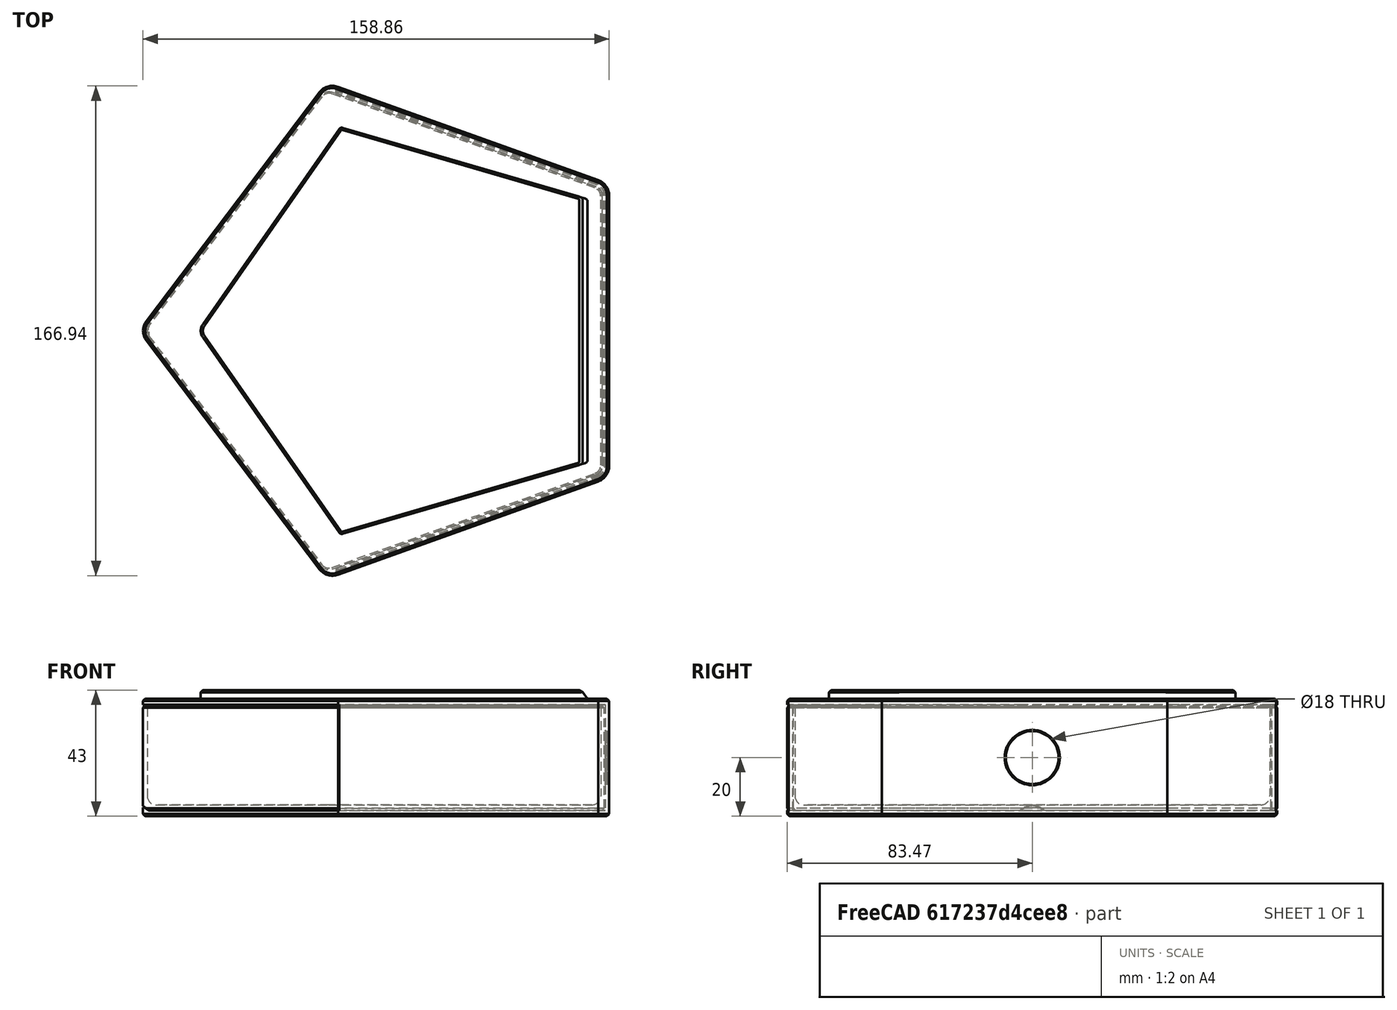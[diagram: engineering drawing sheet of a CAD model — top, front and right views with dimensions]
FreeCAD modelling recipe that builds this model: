
FCSTD DOCUMENT  (FreeCAD 1.0R39109 (Git))
Label: storage box
License: All rights reserved
objects: Sketcher::SketchObject×11, PartDesign::Pocket×6, PartDesign::Chamfer×6, PartDesign::Pad×5, PartDesign::SubShapeBinder×3, PartDesign::Fillet×2, PartDesign::Body×2, Mesh::Feature×1, Part::Feature×1, App::VarSet×1
note: 85 computed .brp shape members not serialized (recipe doc carries the construction recipe); baked Part::Feature solids carry a one-line shape summary decoded from their .brp

FEATURE [Mesh::Feature] stand
FEATURE [Part::Feature] stand001
  shape: bbox 160.2 x 168.2 x 43.41 mm, 6068 faces, 0 solids (baked)
FEATURE [Sketcher::SketchObject] Sketch  label="stand_footprint"
  ArcFitTolerance = 1e-06
  ExternalGeometry = -> [stand001]
  FullyConstrained = true
  MakeInternals = false
  sketch-geometry (17):
    g0: Circle [constr] CenterX=106.078 CenterY=95.15 CenterZ=0 NormalX=0 NormalY=0 NormalZ=1 AngleXU=0 Radius=73.5295
    g1: LineSegment StartX=82.4481 StartY=164.779 StartZ=0 EndX=35.3147 EndY=97.3554 EndZ=0
    g2: LineSegment StartX=35.3147 StartY=92.9447 StartZ=0 EndX=82.4481 EndY=25.521 EndZ=0
    g3: LineSegment StartX=82.4481 StartY=25.521 StartZ=0 EndX=166.952 EndY=50.1585 EndZ=0
    g4: LineSegment StartX=166.952 StartY=50.1585 StartZ=0 EndX=166.952 EndY=140.142 EndZ=0
    g5: LineSegment StartX=166.952 StartY=140.142 StartZ=0 EndX=82.4481 EndY=164.779 EndZ=0
    g6: ArcOfCircle CenterX=38.8397 CenterY=95.15 CenterZ=0 NormalX=0 NormalY=0 NormalZ=1 AngleXU=0 Radius=4.15798 StartAngle=2.58254 EndAngle=3.70065
    g7: LineSegment StartX=81.6615 StartY=178.264 StartZ=0 EndX=170.408 EndY=146.468 EndZ=0
    g8: LineSegment StartX=174.094 StartY=141.161 StartZ=0 EndX=174.094 EndY=49.139 EndZ=0
    g9: LineSegment StartX=170.408 StartY=43.8321 StartZ=0 EndX=81.6615 EndY=12.0355 EndZ=0
    g10: LineSegment StartX=75.409 StartY=13.8037 StartZ=0 EndX=16.3247 EndY=91.9295 EndZ=0
    g11: LineSegment StartX=16.3247 StartY=98.3706 StartZ=0 EndX=75.409 EndY=176.496 EndZ=0
    g12: ArcOfCircle CenterX=20.5106 CenterY=95.15 CenterZ=0 NormalX=0 NormalY=0 NormalZ=1 AngleXU=0 Radius=5.28138 StartAngle=2.4858 EndAngle=3.79739
    g13: ArcOfCircle CenterX=79.7221 CenterY=173.184 CenterZ=0 NormalX=0 NormalY=0 NormalZ=1 AngleXU=0 Radius=5.43855 StartAngle=1.20616 EndAngle=2.48661
    g14: ArcOfCircle CenterX=168.527 CenterY=141.227 CenterZ=0 NormalX=0 NormalY=0 NormalZ=1 AngleXU=0 Radius=5.56815 StartAngle=6.27131 EndAngle=7.50937
    g15: ArcOfCircle CenterX=168.451 CenterY=49.1255 CenterZ=0 NormalX=0 NormalY=0 NormalZ=1 AngleXU=0 Radius=5.64348 StartAngle=5.06648 EndAngle=6.28558
    g16: ArcOfCircle CenterX=79.7195 CenterY=17.1072 CenterZ=0 NormalX=0 NormalY=0 NormalZ=1 AngleXU=0 Radius=5.43077 StartAngle=3.7955 EndAngle=5.07809
  constraints (41):
    c: PointOnObject(g-7,g0)
    c: Coincident(g1,g-5)
    c: Coincident(g2,g-7)
    c: Coincident(g3,g2)
    c: Coincident(g3,g-7)
    c: Coincident(g4,g3)
    c: Coincident(g4,g-5)
    c: Coincident(g5,g4)
    c: Coincident(g5,g1)
    c: Coincident(g2,g-6)
    c: Coincident(g1,g-8)
    c: Coincident(g6,g1)
    c: Coincident(g6,g2)
    c: PointOnObject(g-9,g6)
    c: Coincident(g7,g-16)
    c: Coincident(g7,g-17)
    c: Coincident(g8,g-18)
    c: Coincident(g8,g-19)
    c: Coincident(g9,g-10)
    c: Coincident(g9,g-11)
    c: Coincident(g10,g-12)
    c: Coincident(g10,g-13)
    c: Tangent(g10,g0)
    c: Coincident(g11,g-14)
    c: Coincident(g11,g-15)
    c: Tangent(g11,g0)
    c: Coincident(g12,g10)
    c: Coincident(g12,g11)
    c: PointOnObject(g-24,g12)
    c: Coincident(g13,g11)
    c: Coincident(g13,g7)
    c: PointOnObject(g-20,g13)
    c: Coincident(g14,g7)
    c: Coincident(g14,g8)
    c: PointOnObject(g-21,g14)
    c: Coincident(g15,g9)
    c: Coincident(g15,g8)
    c: PointOnObject(g-22,g15)
    c: Coincident(g16,g10)
    c: Coincident(g16,g9)
    c: PointOnObject(g-23,g16)
FEATURE [Sketcher::SketchObject] Sketch001
  ArcFitTolerance = 1e-06
  AttachmentSupport = -> [XY_Plane]
  ExternalGeometry = -> [stand001]
  FullyConstrained = true
  MakeInternals = false
  MapMode = 5
  sketch-geometry (11):
    g0: Circle [constr] CenterX=106.078 CenterY=95.15 CenterZ=0 NormalX=0 NormalY=0 NormalZ=1 AngleXU=0 Radius=73.5295
    g1: LineSegment StartX=81.6615 StartY=178.264 StartZ=0 EndX=170.408 EndY=146.468 EndZ=0
    g2: LineSegment StartX=174.094 StartY=141.161 StartZ=0 EndX=174.094 EndY=49.139 EndZ=0
    g3: LineSegment StartX=170.408 StartY=43.8321 StartZ=0 EndX=81.6615 EndY=12.0355 EndZ=0
    g4: LineSegment StartX=75.409 StartY=13.8037 StartZ=0 EndX=16.3247 EndY=91.9295 EndZ=0
    g5: LineSegment StartX=16.3247 StartY=98.3706 StartZ=0 EndX=75.409 EndY=176.496 EndZ=0
    g6: ArcOfCircle CenterX=20.5106 CenterY=95.15 CenterZ=0 NormalX=0 NormalY=0 NormalZ=1 AngleXU=0 Radius=5.28138 StartAngle=2.4858 EndAngle=3.79739
    g7: ArcOfCircle CenterX=79.7221 CenterY=173.184 CenterZ=0 NormalX=0 NormalY=0 NormalZ=1 AngleXU=0 Radius=5.43855 StartAngle=1.20616 EndAngle=2.48661
    g8: ArcOfCircle CenterX=168.527 CenterY=141.227 CenterZ=0 NormalX=0 NormalY=0 NormalZ=1 AngleXU=0 Radius=5.56815 StartAngle=6.27131 EndAngle=7.50937
    g9: ArcOfCircle CenterX=168.451 CenterY=49.1255 CenterZ=0 NormalX=0 NormalY=0 NormalZ=1 AngleXU=0 Radius=5.64348 StartAngle=5.06648 EndAngle=6.28558
    g10: ArcOfCircle CenterX=79.7195 CenterY=17.1072 CenterZ=0 NormalX=0 NormalY=0 NormalZ=1 AngleXU=0 Radius=5.43077 StartAngle=3.7955 EndAngle=5.07809
  constraints (28):
    c: PointOnObject(g-7,g0)
    c: Coincident(g1,g-16)
    c: Coincident(g1,g-17)
    c: Coincident(g2,g-18)
    c: Coincident(g2,g-19)
    c: Coincident(g3,g-10)
    c: Coincident(g3,g-11)
    c: Coincident(g4,g-12)
    c: Coincident(g4,g-13)
    c: Tangent(g4,g0)
    c: Coincident(g5,g-14)
    c: Coincident(g5,g-15)
    c: Tangent(g5,g0)
    c: Coincident(g6,g4)
    c: Coincident(g6,g5)
    c: PointOnObject(g-24,g6)
    c: Coincident(g7,g5)
    c: Coincident(g7,g1)
    c: PointOnObject(g-20,g7)
    c: Coincident(g8,g1)
    c: Coincident(g8,g2)
    c: PointOnObject(g-21,g8)
    c: Coincident(g9,g3)
    c: Coincident(g9,g2)
    c: PointOnObject(g-22,g9)
    c: Coincident(g10,g4)
    c: Coincident(g10,g3)
    c: PointOnObject(g-23,g10)
FEATURE [App::VarSet] VarSet001  label="dim"
  Height = 40
  back_hole = 18
  lip_height = 3
  wall = 1.3
FEATURE [PartDesign::Pad] Pad
  Direction = (0,0,1)
  Length = 40
  Length2 = 10
  Profile = -> Sketch001
  ReferenceAxis = -> Sketch001 [N_Axis]
  Refine = true
  Reversed = true
  Suppressed = false
  Type = 0
  expr: Length = VarSet001.Height
FEATURE [Sketcher::SketchObject] Sketch002
  ArcFitTolerance = 1e-06
  AttachmentSupport = -> [XY_Plane]
  ExternalGeometry = -> [stand001]
  FullyConstrained = true
  MakeInternals = false
  MapMode = 5
  sketch-geometry (20):
    g0: LineSegment [constr] StartX=82.4481 StartY=164.779 StartZ=0 EndX=35.3147 EndY=97.3554 EndZ=0
    g1: LineSegment [constr] StartX=35.3147 StartY=92.9447 StartZ=0 EndX=82.4481 EndY=25.521 EndZ=0
    g2: LineSegment [constr] StartX=82.4481 StartY=25.521 StartZ=0 EndX=166.952 EndY=50.1585 EndZ=0
    g3: LineSegment [constr] StartX=166.952 StartY=50.1585 StartZ=0 EndX=166.952 EndY=140.142 EndZ=0
    g4: ArcOfCircle [constr] CenterX=38.8397 CenterY=95.15 CenterZ=0 NormalX=0 NormalY=0 NormalZ=1 AngleXU=0 Radius=4.15798 StartAngle=2.58254 EndAngle=3.70065
    g5: LineSegment [constr] StartX=82.4481 StartY=164.779 StartZ=0 EndX=166.952 EndY=140.142 EndZ=0
    g6: LineSegment StartX=82.5298 StartY=164.547 StartZ=0 EndX=166.752 EndY=139.991 EndZ=0
    g7: LineSegment StartX=166.752 StartY=50.3085 StartZ=0 EndX=166.752 EndY=139.991 EndZ=0
    g8: LineSegment StartX=82.5298 StartY=25.7532 StartZ=0 EndX=166.752 EndY=50.3085 EndZ=0
    g9: LineSegment StartX=35.6002 StartY=92.8854 StartZ=0 EndX=82.5298 EndY=25.7532 EndZ=0
    g10: ArcOfCircle CenterX=38.8397 CenterY=95.15 CenterZ=0 NormalX=0 NormalY=0 NormalZ=1 AngleXU=0 Radius=3.95256 StartAngle=2.5315 EndAngle=3.75169
    g11: LineSegment StartX=82.5298 StartY=164.547 StartZ=0 EndX=35.6002 EndY=97.4146 EndZ=0
    g12: LineSegment [constr] StartX=166.752 StartY=139.991 StartZ=0 EndX=166.952 EndY=139.991 EndZ=0
    g13: LineSegment [constr] StartX=166.752 StartY=139.991 StartZ=0 EndX=166.808 EndY=140.183 EndZ=0
    g14: LineSegment [constr] StartX=82.5298 StartY=164.547 StartZ=0 EndX=82.5858 EndY=164.739 EndZ=0
    g15: LineSegment [constr] StartX=82.5298 StartY=164.547 StartZ=0 EndX=82.3659 EndY=164.661 EndZ=0
    g16: LineSegment [constr] StartX=166.752 StartY=50.3085 StartZ=0 EndX=166.952 EndY=50.3085 EndZ=0
    g17: LineSegment [constr] StartX=166.752 StartY=50.3085 StartZ=0 EndX=166.808 EndY=50.1165 EndZ=0
    g18: LineSegment [constr] StartX=82.5298 StartY=25.7532 StartZ=0 EndX=82.5858 EndY=25.5612 EndZ=0
    g19: LineSegment [constr] StartX=82.5298 StartY=25.7532 StartZ=0 EndX=82.3659 EndY=25.6386 EndZ=0
  constraints (53):
    c: Coincident(g1,g-6)
    c: Coincident(g2,g1)
    c: Coincident(g3,g-4)
    c: Coincident(g1,g-5)
    c: Coincident(g0,g-7)
    c: Coincident(g4,g0)
    c: Coincident(g4,g1)
    c: PointOnObject(g-8,g4)
    c: Coincident(g5,g0)
    c: Coincident(g5,g3)
    c: Coincident(g0,g-7)
    c: Coincident(g6,g7)
    c: Coincident(g6,g11)
    c: Coincident(g7,g8)
    c: Coincident(g8,g9)
    c: Coincident(g12,g6)
    c: PointOnObject(g12,g3)
    c: Perpendicular(g3,g12)
    c: Distance(g12,g12) = 0.2
    c: Coincident(g13,g6)
    c: PointOnObject(g13,g5)
    c: Perpendicular(g5,g13)
    c: Equal(g13,g12)
    c: Parallel(g6,g5)
    c: Parallel(g11,g0)
    c: Coincident(g14,g6)
    c: PointOnObject(g14,g5)
    c: Coincident(g15,g6)
    c: PointOnObject(g15,g0)
    c: Perpendicular(g15,g0)
    c: Perpendicular(g5,g14)
    c: Equal(g14,g15)
    c: Parallel(g3,g7)
    c: Coincident(g16,g7)
    c: PointOnObject(g16,g3)
    c: Horizontal(g16)
    c: Coincident(g17,g7)
    c: PointOnObject(g17,g2)
    c: Perpendicular(g2,g17)
    c: Equal(g17,g16)
    c: Parallel(g8,g2)
    c: Parallel(g9,g1)
    c: Coincident(g2,g3)
    c: Coincident(g2,g-6)
    c: Coincident(g18,g8)
    c: PointOnObject(g18,g2)
    c: Coincident(g19,g8)
    c: PointOnObject(g19,g1)
    c: Perpendicular(g19,g1)
    c: Perpendicular(g2,g18)
    c: Coincident(g4,g10)
    c: Tangent(g9,g10) = -1.5708
    c: Tangent(g10,g11) = -1.5708
FEATURE [PartDesign::Pad] Pad001
  BaseFeature = -> Pad
  Direction = (0,0,1)
  Length = 3
  Length2 = 10
  Profile = -> Sketch002
  ReferenceAxis = -> Sketch002 [N_Axis]
  Refine = true
  Suppressed = false
  Type = 0
  expr: Length = VarSet001.lip_height
FEATURE [Sketcher::SketchObject] Sketch003
  ArcFitTolerance = 1e-06
  AttachmentOffset = pos=(0,0,-2) rot=(0,0,1;0rad)
  FullyConstrained = true
  MakeInternals = false
  MapMode = 5
  Placement = pos=(0,0,-38) rot=(1,0,0;3.14159rad)
  expr: Constraints[27] = VarSet001.wall
  sketch-geometry (14):
    g0: LineSegment StartX=81.6615 StartY=-3.49618 StartZ=0 EndX=81.6615 EndY=-13.4962 EndZ=0
    g1: LineSegment StartX=81.6615 StartY=-13.4962 StartZ=0 EndX=169.891 EndY=-45.1074 EndZ=0
    g2: LineSegment StartX=172.719 StartY=-49.122 StartZ=0 EndX=172.795 EndY=-141.224 EndZ=0
    g3: LineSegment StartX=169.966 StartY=-145.245 StartZ=0 EndX=81.6615 EndY=-176.884 EndZ=0
    g4: LineSegment StartX=81.6615 StartY=-176.884 StartZ=0 EndX=81.6615 EndY=-186.884 EndZ=0
    g5: LineSegment StartX=81.6615 StartY=-186.884 StartZ=0 EndX=0 EndY=-186.884 EndZ=0
    g6: LineSegment StartX=0 StartY=-186.884 StartZ=0 EndX=0 EndY=-3.49618 EndZ=0
    g7: LineSegment StartX=0 StartY=-3.49618 StartZ=0 EndX=81.6615 EndY=-3.49618 EndZ=0
    g8: ArcOfCircle CenterX=168.527 CenterY=-141.227 CenterZ=0 NormalX=0 NormalY=0 NormalZ=1 AngleXU=0 Radius=4.26815 StartAngle=5.05643 EndAngle=6.28401
    g9: GeomPoint [constr] X=172.797 Y=-144.231 Z=0
    g10: ArcOfCircle CenterX=168.451 CenterY=-49.1255 CenterZ=0 NormalX=0 NormalY=0 NormalZ=1 AngleXU=0 Radius=4.26815 StartAngle=0.000821981 EndAngle=1.22676
    g11: GeomPoint [constr] X=172.717 Y=-46.12 Z=0
    g12: LineSegment [constr] StartX=81.6615 StartY=-176.884 StartZ=0 EndX=81.6615 EndY=-178.264 EndZ=0
    g13: LineSegment [constr] StartX=81.6615 StartY=-176.884 StartZ=0 EndX=82.1 EndY=-178.107 EndZ=0
  constraints (35):
    c: Vertical(g0)
    c: Coincident(g0,g1)
    c: Coincident(g3,g4)
    c: Vertical(g4)
    c: Coincident(g4,g5)
    c: PointOnObject(g5,g-2)
    c: Horizontal(g5)
    c: Coincident(g5,g6)
    c: PointOnObject(g6,g-2)
    c: Coincident(g6,g7)
    c: Coincident(g7,g0)
    c: Horizontal(g7)
    c: PointOnObject(g9,g3)
    c: PointOnObject(g9,g2)
    c: Tangent(g3,g8) = 1.5708
    c: Tangent(g2,g8) = 1.5708
    c: PointOnObject(g11,g1)
    c: PointOnObject(g11,g2)
    c: Tangent(g1,g10) = 1.5708
    c: Tangent(g2,g10) = 1.5708
    c: PointOnObject(g-7,g4)
    c: Coincident(g12,g3)
    c: Coincident(g12,g-7)
    c: Coincident(g13,g3)
    c: PointOnObject(g13,g-7)
    c: Perpendicular(g-7,g13)
    c: Parallel(g-7,g3)
    c: Distance(g13,g13) = 1.3
    c: Coincident(g8,g-6)
    c: Coincident(g10,g-4)
    c: Equal(g10,g8)
    c: Parallel(g1,g-3)
    c: PointOnObject(g-3,g0)
    c: Equal(g0,g4)
    c: DistanceY(g4,g4) = 10
FEATURE [PartDesign::Pocket] Pocket
  BaseFeature = -> Pad001
  Direction = (0,0,1)
  Length = 36
  Length2 = 5
  Profile = -> Sketch003
  ReferenceAxis = -> Sketch003 [N_Axis]
  Refine = true
  Suppressed = false
  Type = 0
  expr: Length = Pad.Length - 2 * 2 mm
FEATURE [Sketcher::SketchObject] Sketch004
  ArcFitTolerance = 1e-06
  AttachmentSupport = -> [Pocket]
  ExternalGeometry = -> [Pocket]
  FullyConstrained = true
  MakeInternals = false
  MapMode = 5
  Placement = pos=(174.094,0,0) rot=(0.57735,0.57735,0.57735;2.0944rad)
  expr: Constraints[1] = VarSet001.back_hole
  sketch-geometry (1):
    g0: Circle CenterX=95.15 CenterY=-20 CenterZ=0 NormalX=0 NormalY=0 NormalZ=1 AngleXU=0 Radius=9
  constraints (2):
    c: Symmetric(g-4,g-3,g0)
    c: Diameter(g0) = 18
FEATURE [PartDesign::Pocket] Pocket001
  BaseFeature = -> Pocket
  Direction = (-1,0,0)
  Length = 5
  Length2 = 5
  Profile = -> Sketch004
  ReferenceAxis = -> Sketch004 [N_Axis]
  Refine = true
  Suppressed = false
  Type = 1
FEATURE [PartDesign::SubShapeBinder] Binder
  BindCopyOnChange = 0
  BindMode = 0
  ClaimChildren = false
  Context = -> Body001 [Binder.]
  Fuse = false
  MakeFace = true
  OffsetFill = false
  OffsetIntersection = false
  OffsetJoinType = 0
  OffsetOpenResult = false
  PartialLoad = false
  Refine = true
  Relative = true
  Support = -> [Body[Pocket001.Face31]]
  _Version = 2
FEATURE [PartDesign::SubShapeBinder] Binder001
  BindCopyOnChange = 0
  BindMode = 0
  ClaimChildren = false
  Context = -> Body001 [Binder001.]
  Fuse = false
  MakeFace = true
  OffsetFill = false
  OffsetIntersection = false
  OffsetJoinType = 0
  OffsetOpenResult = false
  PartialLoad = false
  Refine = true
  Relative = true
  Support = -> [Body[Pocket001.Face4]]
  _Version = 2
FEATURE [Sketcher::SketchObject] Sketch005
  ArcFitTolerance = 1e-06
  AttachmentSupport = -> [Binder]
  ExternalGeometry = -> [Binder]
  FullyConstrained = true
  MakeInternals = false
  MapMode = 5
  Placement = pos=(0,0,-38) rot=(0,0,1;0rad)
  sketch-geometry (13):
    g0: LineSegment StartX=81.6615 StartY=176.484 StartZ=0 EndX=169.84 EndY=144.891 EndZ=0
    g1: LineSegment StartX=172.419 StartY=141.227 StartZ=0 EndX=172.419 EndY=49.1255 EndZ=0
    g2: LineSegment StartX=75.409 StartY=13.8037 StartZ=0 EndX=16.3247 EndY=91.9295 EndZ=0
    g3: LineSegment StartX=16.3247 StartY=98.3706 StartZ=0 EndX=75.409 EndY=176.496 EndZ=0
    g4: LineSegment StartX=81.6615 StartY=13.8149 StartZ=0 EndX=169.789 EndY=45.3899 EndZ=0
    g5: LineSegment [constr] StartX=81.6615 StartY=13.8149 StartZ=0 EndX=81.7627 EndY=13.5324 EndZ=0
    g6: LineSegment StartX=81.6615 StartY=13.8149 StartZ=0 EndX=81.6615 EndY=12.0355 EndZ=0
    g7: ArcOfCircle CenterX=168.451 CenterY=49.1255 CenterZ=0 NormalX=0 NormalY=0 NormalZ=1 AngleXU=0 Radius=3.96815 StartAngle=5.05643 EndAngle=6.28319
    g8: ArcOfCircle CenterX=168.527 CenterY=141.227 CenterZ=0 NormalX=0 NormalY=0 NormalZ=1 AngleXU=0 Radius=3.89244 StartAngle=-9e-16 EndAngle=1.22676
    g9: ArcOfCircle CenterX=79.7221 CenterY=173.184 CenterZ=0 NormalX=0 NormalY=0 NormalZ=1 AngleXU=0 Radius=5.43855 StartAngle=1.20616 EndAngle=2.48661
    g10: LineSegment StartX=81.6615 StartY=176.484 StartZ=0 EndX=81.6615 EndY=178.264 EndZ=0
    g11: ArcOfCircle CenterX=20.5106 CenterY=95.15 CenterZ=0 NormalX=0 NormalY=0 NormalZ=1 AngleXU=0 Radius=5.28138 StartAngle=2.4858 EndAngle=3.79739
    g12: ArcOfCircle CenterX=79.7195 CenterY=17.1072 CenterZ=0 NormalX=0 NormalY=0 NormalZ=1 AngleXU=0 Radius=5.43077 StartAngle=3.7955 EndAngle=5.07809
  constraints (32):
    c: Vertical(g1)
    c: Coincident(g2,g-9)
    c: Coincident(g2,g-8)
    c: Coincident(g3,g-8)
    c: Coincident(g3,g-10)
    c: Parallel(g4,g-3)
    c: Coincident(g5,g4)
    c: PointOnObject(g5,g-3)
    c: Perpendicular(g-3,g5)
    c: Distance(g5,g5) = 0.3
    c: Coincident(g6,g4)
    c: Coincident(g6,g-9)
    c: Vertical(g6)
    c: Coincident(g7,g-12)
    c: Coincident(g8,g-11)
    c: Parallel(g0,g-5)
    c: Coincident(g9,g-10)
    c: Coincident(g9,g3)
    c: Tangent(g8,g0) = 1.5708
    c: Tangent(g8,g1) = 1.5708
    c: Tangent(g7,g1) = 1.5708
    c: Tangent(g7,g4) = -1.5708
    c: Vertical(g9,g0)
    c: Vertical(g0,g-5)
    c: Coincident(g10,g0)
    c: Coincident(g10,g9)
    c: Coincident(g11,g2)
    c: Coincident(g11,g3)
    c: Coincident(g12,g2)
    c: Coincident(g12,g6)
    c: Equal(g12,g-9)
    c: Coincident(g11,g-8)
FEATURE [PartDesign::Pad] Pad002
  Direction = (0,0,1)
  Length = 35.5
  Length2 = 10
  Profile = -> Sketch005
  ReferenceAxis = -> Sketch005 [N_Axis]
  Refine = true
  Suppressed = false
  Type = 0
  expr: Length = <<Pocket>>.Length - 0.5 mm
FEATURE [PartDesign::SubShapeBinder] Binder002
  BindCopyOnChange = 0
  BindMode = 0
  ClaimChildren = false
  Context = -> Body [Binder002.]
  Fuse = false
  MakeFace = true
  OffsetFill = false
  OffsetIntersection = false
  OffsetJoinType = 0
  OffsetOpenResult = false
  PartialLoad = false
  Refine = true
  Relative = true
  Support = -> [Pocket[Face30]]
  _Version = 2
FEATURE [Sketcher::SketchObject] Sketch006
  ArcFitTolerance = 1e-06
  AttachmentSupport = -> [Binder002]
  ExternalGeometry = -> [Pocket]
  FullyConstrained = true
  MakeInternals = false
  MapMode = 5
  Placement = pos=(0,0,-38) rot=(0,0,1;0rad)
  sketch-geometry (8):
    g0: LineSegment StartX=81.6615 StartY=176.884 StartZ=0 EndX=83.348 EndY=181.591 EndZ=0
    g1: LineSegment StartX=83.348 StartY=181.591 StartZ=0 EndX=78.641 EndY=183.277 EndZ=0
    g2: LineSegment StartX=78.641 StartY=183.277 StartZ=0 EndX=76.9545 EndY=178.57 EndZ=0
    g3: LineSegment StartX=76.9545 StartY=178.57 StartZ=0 EndX=81.6615 EndY=176.884 EndZ=0
    g4: LineSegment StartX=81.6615 StartY=13.4962 StartZ=0 EndX=83.348 EndY=8.78918 EndZ=0
    g5: LineSegment StartX=83.348 StartY=8.78918 StartZ=0 EndX=78.641 EndY=7.10272 EndZ=0
    g6: LineSegment StartX=78.641 StartY=7.10272 StartZ=0 EndX=76.9545 EndY=11.8097 EndZ=0
    g7: LineSegment StartX=76.9545 StartY=11.8097 StartZ=0 EndX=81.6615 EndY=13.4962 EndZ=0
  constraints (22):
    c: Coincident(g0,g-3)
    c: Coincident(g1,g0)
    c: Coincident(g2,g1)
    c: Coincident(g3,g2)
    c: Coincident(g3,g0)
    c: Perpendicular(g2,g3)
    c: Perpendicular(g1,g2)
    c: Perpendicular(g0,g1)
    c: Equal(g3,g0)
    c: Perpendicular(g-4,g0)
    c: Distance(g0,g0) = 5
    c: Coincident(g-5,g4)
    c: Coincident(g4,g5)
    c: Coincident(g5,g6)
    c: Coincident(g6,g7)
    c: Coincident(g7,g4)
    c: Perpendicular(g-6,g4)
    c: Perpendicular(g5,g4)
    c: Perpendicular(g6,g5)
    c: Perpendicular(g7,g6)
    c: Equal(g5,g4)
    c: Equal(g4,g0)
FEATURE [PartDesign::Pocket] Pocket002
  BaseFeature = -> Pocket001
  Direction = (0,0,-1)
  Length = 0
  Length2 = 5
  Profile = -> Sketch006
  ReferenceAxis = -> Sketch006 [N_Axis]
  Refine = true
  Suppressed = false
  Type = 3
  UpToFace = -> Pocket001 [Face4]
FEATURE [Sketcher::SketchObject] Sketch007
  ArcFitTolerance = 1e-06
  AttachmentSupport = -> [XZ_Plane001]
  ExternalGeometry = -> [Pad002]
  FullyConstrained = true
  MakeInternals = false
  MapMode = 5
  Placement = pos=(0,0,0) rot=(1,0,0;1.5708rad)
  sketch-geometry (3):
    g0: LineSegment StartX=15.2292 StartY=-36.5 StartZ=0 EndX=15.2292 EndY=-38 EndZ=0
    g1: LineSegment StartX=15.2292 StartY=-38 StartZ=0 EndX=17.3714 EndY=-38 EndZ=0
    g2: LineSegment StartX=17.3714 StartY=-38 StartZ=0 EndX=15.2292 EndY=-36.5 EndZ=0
  constraints (9):
    c: Coincident(g0,g1)
    c: Horizontal(g1)
    c: Coincident(g1,g2)
    c: Coincident(g2,g0)
    c: Angle(g2,g-3) = 0.610865
    c: Vertical(g0)
    c: DistanceX(g0,g-3) = 0
    c: DistanceY(g0,g-3) = 0
    c: DistanceY(g0,g0) = 1.5
FEATURE [Sketcher::SketchObject] Sketch008
  ArcFitTolerance = 1e-06
  AttachmentSupport = -> [XZ_Plane]
  ExternalGeometry = -> [Pocket002,Binder002]
  FullyConstrained = true
  MakeInternals = false
  MapMode = 5
  Placement = pos=(0,0,0) rot=(1,0,0;1.5708rad)
  sketch-geometry (6):
    g0: LineSegment [constr] StartX=15.2292 StartY=-38 StartZ=0 EndX=15.2292 EndY=-36.7 EndZ=0
    g1: LineSegment [constr] StartX=15.2292 StartY=-36.7 StartZ=0 EndX=17.0858 EndY=-38 EndZ=0
    g2: LineSegment StartX=17.0858 StartY=-38 StartZ=0 EndX=15.2292 EndY=-38 EndZ=0
    g3: LineSegment StartX=15.2292 StartY=-38 StartZ=0 EndX=15.2292 EndY=-37 EndZ=0
    g4: LineSegment StartX=15.2292 StartY=-37 StartZ=0 EndX=15.6576 EndY=-37 EndZ=0
    g5: LineSegment StartX=15.6576 StartY=-37 StartZ=0 EndX=17.0858 EndY=-38 EndZ=0
  constraints (16):
    c: Coincident(g0,g-3)
    c: Vertical(g0)
    c: Coincident(g1,g0)
    c: PointOnObject(g1,g-4)
    c: Coincident(g2,g1)
    c: Coincident(g2,g0)
    c: Angle(g1) = -0.610865
    c: DistanceY(g0,g0) = 1.3
    c: Coincident(g3,g0)
    c: PointOnObject(g3,g0)
    c: Coincident(g4,g3)
    c: PointOnObject(g4,g1)
    c: Horizontal(g4)
    c: Coincident(g5,g4)
    c: Coincident(g5,g1)
    c: Distance(g3,g0) = 0.3
FEATURE [PartDesign::Pad] Pad003
  BaseFeature = -> Pocket002
  Direction = (0,-1,2e-16)
  Length = 120
  Length2 = 10
  Profile = -> Sketch008
  ReferenceAxis = -> Sketch008 [N_Axis]
  Refine = true
  Reversed = true
  Suppressed = false
  Type = 0
FEATURE [Sketcher::SketchObject] Sketch009
  ArcFitTolerance = 1e-06
  AttachmentSupport = -> [XY_Plane]
  ExternalGeometry = -> [Pad003]
  FullyConstrained = false
  MakeInternals = false
  MapMode = 5
  sketch-geometry (7):
    g0: LineSegment StartX=75.409 StartY=176.496 StartZ=0 EndX=16.3247 EndY=98.3706 EndZ=0
    g1: LineSegment StartX=16.3247 StartY=91.9295 StartZ=0 EndX=75.409 EndY=13.8037 EndZ=0
    g2: ArcOfCircle CenterX=20.5106 CenterY=95.15 CenterZ=0 NormalX=0 NormalY=0 NormalZ=1 AngleXU=0 Radius=5.28138 StartAngle=2.4858 EndAngle=3.79739
    g3: LineSegment StartX=75.409 StartY=13.8037 StartZ=0 EndX=75.409 EndY=-36.8987 EndZ=0
    g4: LineSegment StartX=75.409 StartY=-36.8987 StartZ=0 EndX=-48.1023 EndY=-36.8987 EndZ=0
    g5: LineSegment StartX=-48.1023 StartY=-36.8987 StartZ=0 EndX=-48.1023 EndY=176.496 EndZ=0
    g6: LineSegment StartX=-48.1023 StartY=176.496 StartZ=0 EndX=75.409 EndY=176.496 EndZ=0
  constraints (16):
    c: Coincident(g0,g-3)
    c: Coincident(g0,g-5)
    c: Coincident(g1,g-5)
    c: Coincident(g1,g-4)
    c: Coincident(g2,g1)
    c: Coincident(g2,g0)
    c: Equal(g-5,g2)
    c: Coincident(g1,g3)
    c: Vertical(g3)
    c: Coincident(g3,g4)
    c: Horizontal(g4)
    c: Coincident(g4,g5)
    c: Vertical(g5)
    c: Coincident(g5,g6)
    c: Coincident(g6,g0)
    c: Horizontal(g6)
FEATURE [PartDesign::Pad] Pad004
  BaseFeature = -> Pad003
  Direction = (0,0,1)
  Length = 100
  Length2 = 10
  Midplane = true
  Profile = -> Sketch009
  ReferenceAxis = -> Sketch009 [N_Axis]
  Refine = true
  Suppressed = false
  Type = 0
FEATURE [PartDesign::Pocket] Pocket004
  BaseFeature = -> Pad004
  Direction = (0,0,-1)
  Length = 100
  Length2 = 5
  Midplane = true
  Profile = -> Sketch009
  ReferenceAxis = -> Sketch009 [N_Axis]
  Refine = true
  Suppressed = false
  Type = 0
FEATURE [Sketcher::SketchObject] Sketch010
  ArcFitTolerance = 1e-06
  AttachmentSupport = -> [Binder001]
  ExternalGeometry = -> [Binder001]
  FullyConstrained = true
  MakeInternals = false
  MapMode = 5
  Placement = pos=(0,0,-2) rot=(1,0,0;3.14159rad)
  sketch-geometry (10):
    g0: LineSegment StartX=77.492 StartY=-13.7019 StartZ=0 EndX=171.196 EndY=-47.2749 EndZ=0
    g1: LineSegment StartX=171.196 StartY=-47.2749 StartZ=0 EndX=171.196 EndY=-143.105 EndZ=0
    g2: LineSegment StartX=171.196 StartY=-143.105 StartZ=0 EndX=77.5394 EndY=-176.661 EndZ=0
    g3: LineSegment StartX=77.5394 StartY=-176.661 StartZ=0 EndX=15.8952 EndY=-95.15 EndZ=0
    g4: LineSegment StartX=15.8952 StartY=-95.15 StartZ=0 EndX=77.492 EndY=-13.7019 EndZ=0
    g5: LineSegment [constr] StartX=171.196 StartY=-143.105 StartZ=0 EndX=171.736 EndY=-144.611 EndZ=0
    g6: LineSegment [constr] StartX=171.196 StartY=-143.105 StartZ=0 EndX=172.796 EndY=-143.104 EndZ=0
    g7: LineSegment [constr] StartX=77.5394 StartY=-176.661 StartZ=0 EndX=76.2633 EndY=-177.626 EndZ=0
    g8: LineSegment [constr] StartX=171.196 StartY=-47.2749 StartZ=0 EndX=171.736 EndY=-45.7686 EndZ=0
    g9: LineSegment [constr] StartX=15.8952 StartY=-95.15 StartZ=0 EndX=14.619 EndY=-94.1849 EndZ=0
  constraints (30):
    c: Coincident(g1,g0)
    c: Vertical(g1)
    c: Coincident(g2,g1)
    c: Coincident(g3,g2)
    c: Coincident(g4,g3)
    c: Parallel(g-4,g4)
    c: Parallel(g-3,g0)
    c: Parallel(g-6,g2)
    c: Parallel(g-5,g3)
    c: Coincident(g5,g1)
    c: PointOnObject(g5,g-6)
    c: Coincident(g6,g1)
    c: PointOnObject(g6,g-7)
    c: Coincident(g7,g2)
    c: PointOnObject(g7,g-5)
    c: Coincident(g8,g0)
    c: PointOnObject(g8,g-3)
    c: Coincident(g9,g3)
    c: PointOnObject(g9,g-4)
    c: Perpendicular(g-4,g9)
    c: Perpendicular(g-3,g8)
    c: Perpendicular(g-7,g6)
    c: Perpendicular(g-6,g5)
    c: Perpendicular(g-5,g7)
    c: Coincident(g0,g4)
    c: Equal(g9,g7)
    c: Equal(g7,g5)
    c: Equal(g5,g6)
    c: Equal(g6,g8)
    c: Distance(g5,g5) = 1.6
FEATURE [PartDesign::Chamfer] Chamfer
  Angle = 45
  Base = -> Pocket004 [Edge46,Edge91]
  BaseFeature = -> Pocket004
  ChamferType = 0
  FlipDirection = false
  Refine = true
  Size = 0.4
  Size2 = 1
  SupportTransform = false
  Suppressed = false
  UseAllEdges = false
FEATURE [PartDesign::Chamfer] Chamfer001
  Angle = 35
  Base = -> Chamfer [Edge67]
  BaseFeature = -> Chamfer
  ChamferType = 2
  FlipDirection = false
  Refine = true
  Size = 2.99
  Size2 = 1
  SupportTransform = false
  Suppressed = false
  UseAllEdges = false
  expr: Size = <<Pad001>>.Length - 0.01 mm
FEATURE [PartDesign::Fillet] Fillet
  Base = -> Chamfer001 [Edge2,Edge5,Edge10,Edge30]
  BaseFeature = -> Chamfer001
  Radius = 1
  Refine = true
  SupportTransform = false
  Suppressed = false
  UseAllEdges = false
FEATURE [PartDesign::Chamfer] Chamfer002
  Angle = 45
  Base = -> Fillet [Edge33]
  BaseFeature = -> Fillet
  ChamferType = 0
  FlipDirection = false
  Refine = true
  Size = 0.75
  Size2 = 1
  SupportTransform = false
  Suppressed = false
  UseAllEdges = false
FEATURE [PartDesign::Chamfer] Chamfer003
  Angle = 45
  Base = -> Chamfer002 [Edge27,Edge86]
  BaseFeature = -> Chamfer002
  ChamferType = 0
  FlipDirection = false
  Refine = true
  Size = 0.75
  Size2 = 1
  SupportTransform = false
  Suppressed = false
  UseAllEdges = false
FEATURE [PartDesign::Body] Body  label="box"
  AllowCompound = true
  Group = -> [Sketch001,Sketch,Pad,Sketch002,Pad001,Sketch003,Pocket,Sketch004,Pocket001,Binder002,Sketch006,Pocket002,Sketch008,Pad003,Sketch009,Pad004,Pocket004,Chamfer,Chamfer001,Fillet,Chamfer002,Chamfer003]
  Origin = -> Origin
  Tip = -> Chamfer003
FEATURE [PartDesign::Chamfer] Chamfer004
  Angle = 45
  Base = -> Pad002 [Face13]
  BaseFeature = -> Pad002
  ChamferType = 0
  FlipDirection = false
  Refine = true
  Size = 0.75
  Size2 = 1
  SupportTransform = false
  Suppressed = false
  UseAllEdges = false
FEATURE [PartDesign::Pocket] Pocket003
  BaseFeature = -> Chamfer004
  Direction = (0,1,-2e-16)
  Length = 5
  Length2 = 5
  Midplane = true
  Profile = -> Sketch007
  ReferenceAxis = -> Sketch007 [N_Axis]
  Refine = true
  Suppressed = false
  Type = 1
FEATURE [PartDesign::Pocket] Pocket005
  BaseFeature = -> Pocket003
  Direction = (0,0,1)
  Length = 34.1
  Length2 = 5
  Profile = -> Sketch010
  ReferenceAxis = -> Sketch010 [N_Axis]
  Refine = true
  Reversed = true
  Suppressed = false
  Type = 0
  expr: Length = Pad002.Length - 1.4 mm
FEATURE [PartDesign::Fillet] Fillet001
  Base = -> Pocket005 [Face34,Edge66,Edge64,Edge63,Edge68,Edge61]
  BaseFeature = -> Pocket005
  Radius = 3
  Refine = true
  SupportTransform = false
  Suppressed = false
  UseAllEdges = false
FEATURE [PartDesign::Chamfer] Chamfer005
  Angle = 45
  Base = -> Fillet001 [Edge20,Edge21,Edge19,Edge12,Edge1]
  BaseFeature = -> Fillet001
  ChamferType = 0
  FlipDirection = false
  Refine = true
  Size = 0.5
  Size2 = 1
  SupportTransform = false
  Suppressed = false
  UseAllEdges = false
FEATURE [PartDesign::Body] Body001  label="drawer"
  AllowCompound = true
  Group = -> [Binder,Binder001,Sketch005,Pad002,Sketch007,Chamfer004,Pocket003,Sketch010,Pocket005,Fillet001,Chamfer005]
  Origin = -> Origin001
  Tip = -> Chamfer005
